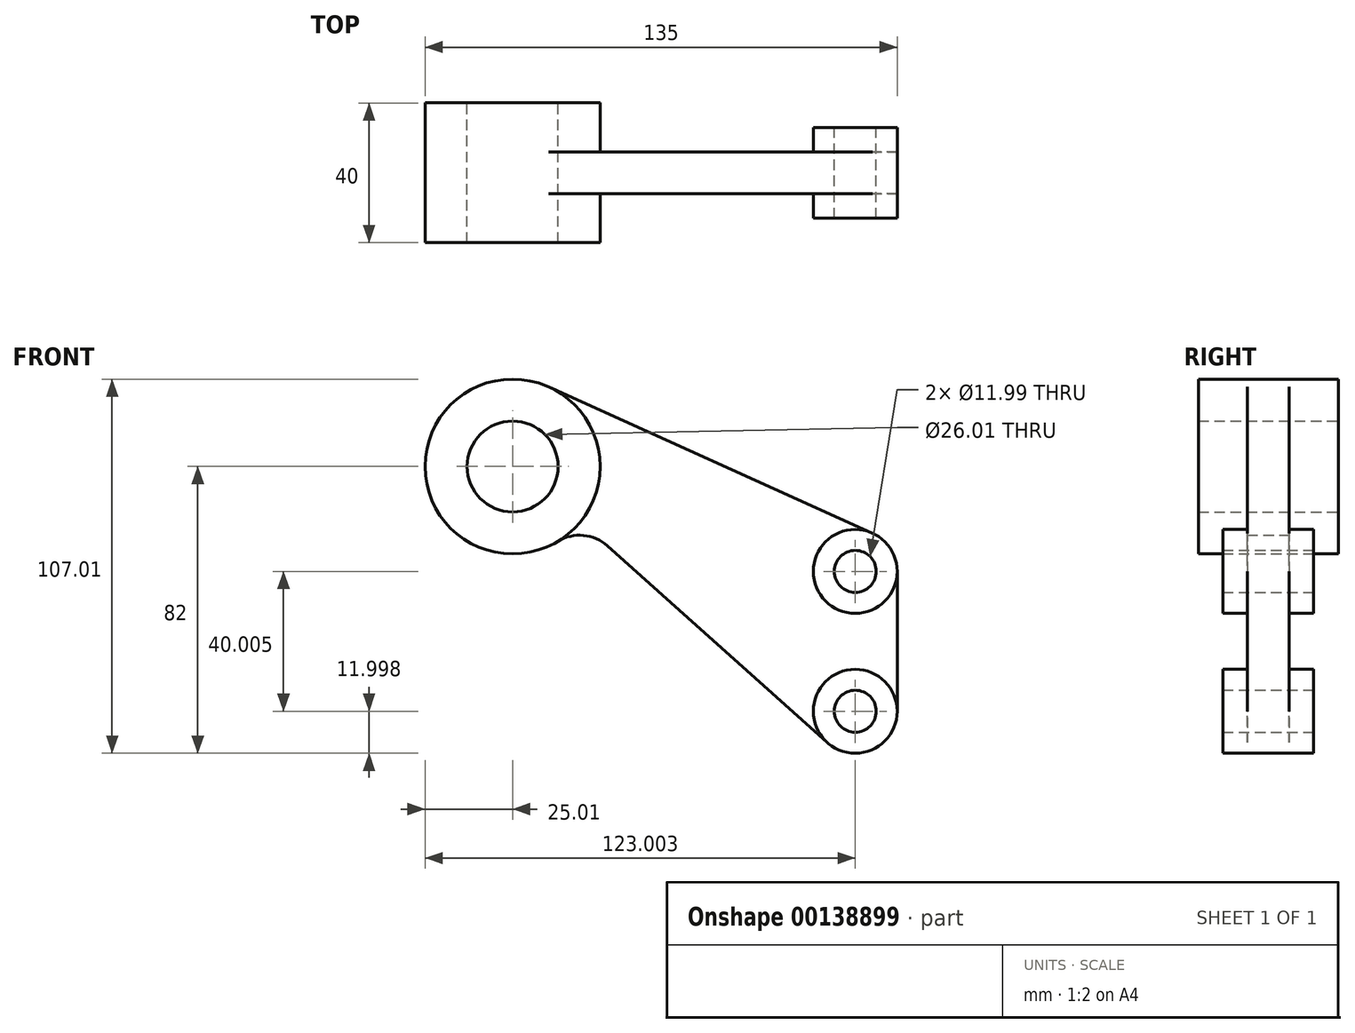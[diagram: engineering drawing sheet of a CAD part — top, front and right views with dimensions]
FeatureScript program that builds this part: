
annotation { "Feature Type Name" : "Feature", "Feature Type Description" : "" }
export const myFeature = defineFeature(function(context is Context, id is Id, definition is map)
    precondition{}
    {
        {
            var Q0;
            Q0=qCreatedBy(makeId("Front.planeOp"),FACE);
            var sketch = newSketch(context, id + "F0", { "sketchPlane" : qUnion([Q0])});
            skCircle(sketch, "E0", {"center": v(0, 0) * mm, "radius": 25 * mm});
            skCircle(sketch, "E1", {"center": v(0, 0) * mm, "radius": 13 * mm});
            skCircle(sketch, "E2", {"center": v(98, -30) * mm, "radius": 12 * mm});
            skCircle(sketch, "E3", {"center": v(98, -30) * mm, "radius": 6 * mm});
            skLineSegment(sketch, "E4", {"start": v(102.93, -19.06) * mm, "end": v(10.3, 22.79) * mm});
            skCircle(sketch, "E5", {"center": v(98, -70) * mm, "radius": 12 * mm});
            skCircle(sketch, "E6", {"center": v(98, -70) * mm, "radius": 6 * mm});
            skLineSegment(sketch, "E7", {"start": v(110, -30) * mm, "end": v(110, -70) * mm});
            skLineSegment(sketch, "E8", {"start": v(90, -78.95) * mm, "end": v(27.15, -22.71) * mm});
            skArc(sketch, "E9", {"start": v(27.15, -22.71) * mm, "mid": v(20.27, -19.71) * mm, "end": v(12.95, -21.4) * mm});
            skSolve(sketch);
        }
        {
            var Q0;
            {var subQ3=sQuery(id+"F0.wireOp",EDGE,"E4");Q0=makeQuery(id+"F0.imprint","IMPRINT",FACE,{"disambiguationData":[TD([[makeQuery(id+"F0.imprint","IMPRINT",EDGE,{"derivedFrom":subQ3}),1.0]])]});}
            extrude(context, id + "F1", {"entities" : qUnion([Q0]), "endBound" : BoundingType.SYMMETRIC, "depth" : 12 * mm});
        }
        {
            var Q0;
            Q0=makeQuery(id+"F0.imprint","IMPRINT",FACE,{"disambiguationData":[TD([[makeQuery(id+"F0.imprint","IMPRINT",EDGE,{"derivedFrom":sQuery(id+"F0.wireOp",EDGE,"E1")}),-1.0]])]});
            extrude(context, id + "F2", {"entities" : qUnion([Q0]), "operationType" : NewBodyOperationType.ADD, "endBound" : BoundingType.SYMMETRIC, "depth" : 40 * mm});
        }
        {
            var Q0;
            Q0=makeQuery(id+"F0.imprint","IMPRINT",FACE,{"disambiguationData":[TD([[makeQuery(id+"F0.imprint","IMPRINT",EDGE,{"derivedFrom":sQuery(id+"F0.wireOp",EDGE,"E3")}),-1.0]])]});
            var Q1;
            Q1=makeQuery(id+"F0.imprint","IMPRINT",FACE,{"disambiguationData":[TD([[makeQuery(id+"F0.imprint","IMPRINT",EDGE,{"derivedFrom":sQuery(id+"F0.wireOp",EDGE,"E6")}),-1.0]])]});
            extrude(context, id + "F3", {"entities" : qUnion([Q0, Q1]), "operationType" : NewBodyOperationType.ADD, "endBound" : BoundingType.SYMMETRIC, "depth" : 26 * mm});
        }
    });
